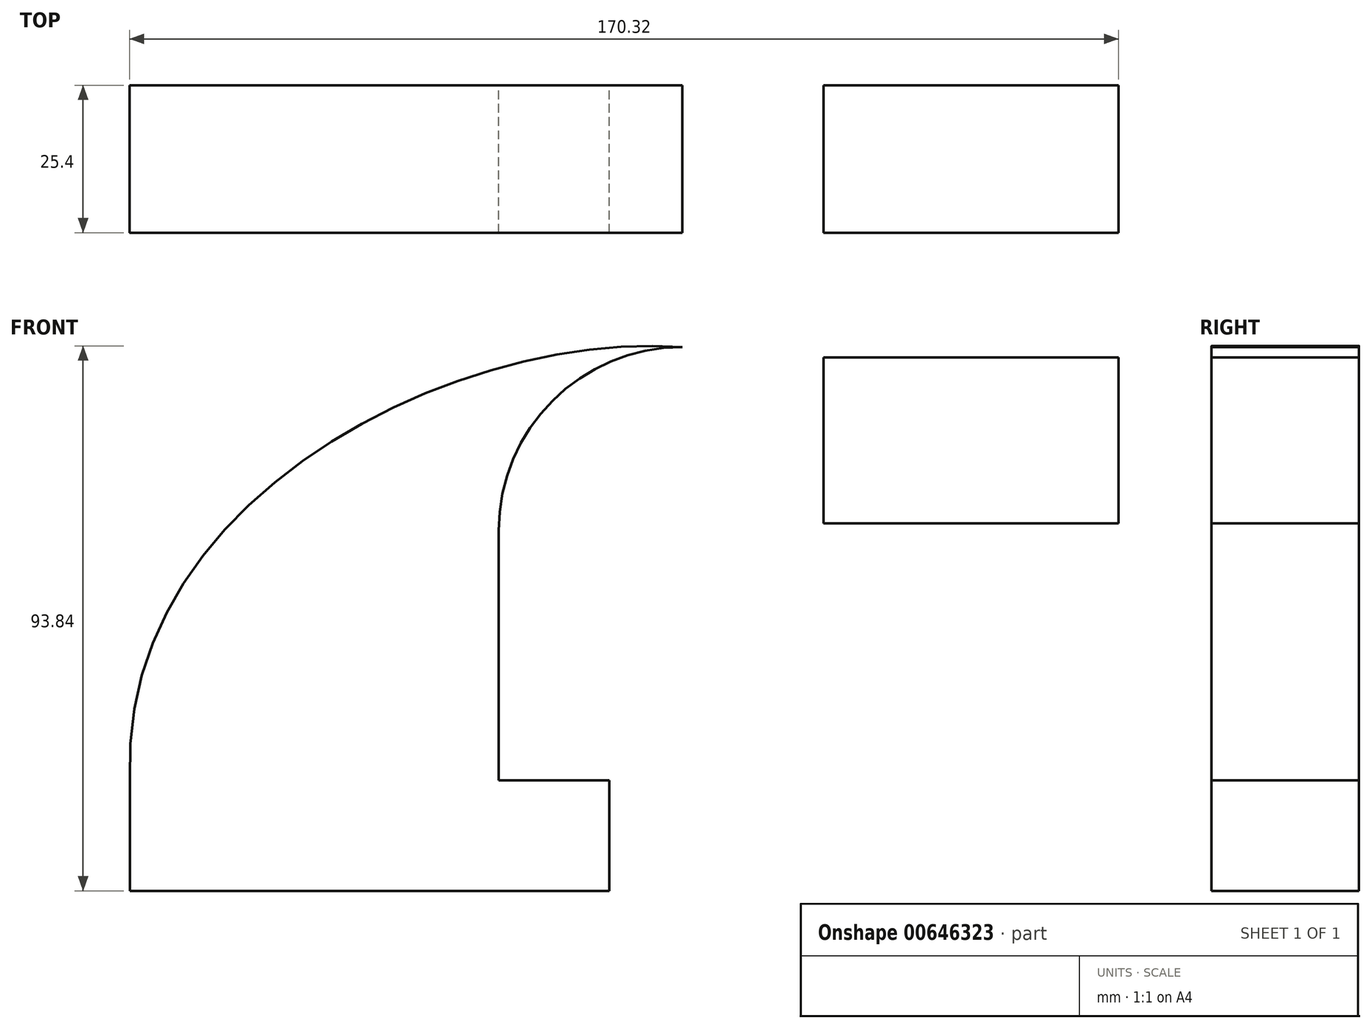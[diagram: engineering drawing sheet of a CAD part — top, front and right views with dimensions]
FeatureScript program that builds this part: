
annotation { "Feature Type Name" : "Feature", "Feature Type Description" : "" }
export const myFeature = defineFeature(function(context is Context, id is Id, definition is map)
    precondition{}
    {
        {
            var Q0;
            Q0=qCreatedBy(makeId("Front.planeOp"),FACE);
            var sketch = newSketch(context, id + "F0", { "sketchPlane" : qUnion([Q0])});
            skLineSegment(sketch, "E0.bottom", {"start": v(-41.28, -9.53) * mm, "end": v(41.28, -9.53) * mm});
            skLineSegment(sketch, "E0.top", {"start": v(-41.28, 9.52) * mm, "end": v(41.28, 9.52) * mm});
            skLineSegment(sketch, "E0.left", {"start": v(-41.27, -9.53) * mm, "end": v(-41.28, 9.52) * mm});
            skLineSegment(sketch, "E0.right", {"start": v(41.28, -9.53) * mm, "end": v(41.28, 9.52) * mm});
            skPoint(sketch, "E0.middle", {"position": v(0, 0) * mm});
            skLineSegment(sketch, "E1.bottom", {"start": v(78.18, 53.73) * mm, "end": v(128.98, 53.73) * mm});
            skLineSegment(sketch, "E1.top", {"start": v(78.18, 82.3) * mm, "end": v(128.98, 82.3) * mm});
            skLineSegment(sketch, "E1.left", {"start": v(78.18, 53.73) * mm, "end": v(78.18, 82.3) * mm});
            skLineSegment(sketch, "E1.right", {"start": v(128.98, 53.73) * mm, "end": v(128.98, 82.3) * mm});
            skPoint(sketch, "E1.middle", {"position": v(103.58, 68.02) * mm});
            skLineSegment(sketch, "E2", {"start": v(41.27, 9.52) * mm, "end": v(41.27, 52.52) * mm});
            skArc(sketch, "E3", {"start": v(41.28, 52.52) * mm, "mid": v(44.95, 61.4) * mm, "end": v(53.82, 65.07) * mm});
            skLineSegment(sketch, "E4", {"start": v(53.82, 65.07) * mm, "end": v(91.3, 65.07) * mm});
            skLineSegment(sketch, "E5.0", {"start": v(53.82, 84.12) * mm, "end": v(91.3, 84.12) * mm});
            skArc(sketch, "E5.1", {"start": v(22.23, 52.52) * mm, "mid": v(31.48, 74.86) * mm, "end": v(53.82, 84.12) * mm});
            skLineSegment(sketch, "E5.2", {"start": v(22.22, 9.52) * mm, "end": v(22.22, 52.52) * mm});
            skLineSegment(sketch, "E6", {"start": v(103.58, 53.73) * mm, "end": v(103.58, 82.3) * mm});
            skFitSpline(sketch, "E7", {"points": [v(-41.28, 9.52) * mm, v(53.82, 84.12) * mm], "startDerivative": vector(-6.78, 146.54) * mm, "endDerivative": vector(116.3, -8.55) * mm});
            skSolve(sketch);
        }
        {
            var Q0;
            Q0 = qSketchRegion(id + "F0", true);
            extrude(context, id + "F1", {"entities" : qUnion([Q0]), "depth" : 25.4 * mm, "offsetDistance" : 25.4 * mm});
        }
    });
